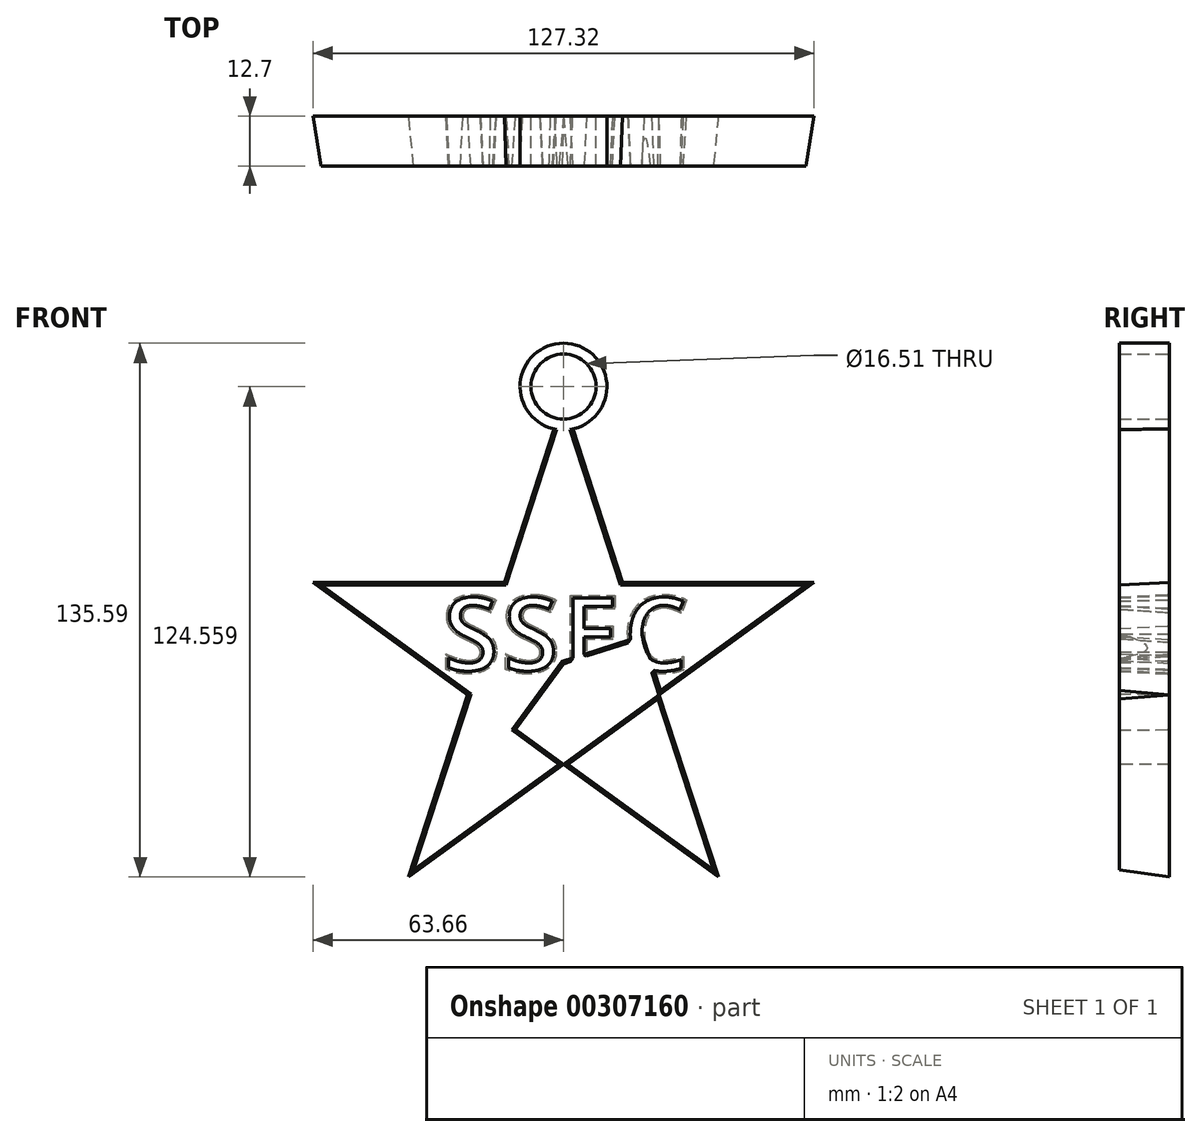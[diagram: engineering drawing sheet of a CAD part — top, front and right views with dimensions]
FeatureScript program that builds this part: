
annotation { "Feature Type Name" : "Feature", "Feature Type Description" : "" }
export const myFeature = defineFeature(function(context is Context, id is Id, definition is map)
    precondition{}
    {
        {
            var Q0;
            Q0=qCreatedBy(makeId("Front.planeOp"),FACE);
            var sketch = newSketch(context, id + "F0", { "sketchPlane" : qUnion([Q0])});
            skLineSegment(sketch, "E0", {"start": v(0, 66.94) * mm, "end": v(-39.35, -54.15) * mm});
            skLineSegment(sketch, "E1", {"start": v(-39.35, -54.15) * mm, "end": v(0, 66.94) * mm});
            skLineSegment(sketch, "E2", {"start": v(0, 66.94) * mm, "end": v(39.35, -54.15) * mm});
            skLineSegment(sketch, "E3", {"start": v(-39.35, -54.15) * mm, "end": v(63.66, 20.68) * mm});
            skLineSegment(sketch, "E4", {"start": v(63.66, 20.68) * mm, "end": v(-63.66, 20.68) * mm});
            skLineSegment(sketch, "E5", {"start": v(-63.66, 20.68) * mm, "end": v(39.35, -54.15) * mm});
            skLineSegment(sketch, "E6", {"start": v(-15.03, 20.68) * mm, "end": v(0, 0) * mm});
            skLineSegment(sketch, "E7", {"start": v(15.03, 20.68) * mm, "end": v(0, 0) * mm});
            skLineSegment(sketch, "E8", {"start": v(0, 0) * mm, "end": v(24.32, -7.9) * mm});
            skLineSegment(sketch, "E9", {"start": v(24.32, -7.9) * mm, "end": v(0, 0) * mm});
            skLineSegment(sketch, "E10", {"start": v(0, -25.57) * mm, "end": v(0, 0) * mm});
            skLineSegment(sketch, "E11", {"start": v(0, 0) * mm, "end": v(-24.32, -7.9) * mm});
            skLineSegment(sketch, "E12", {"start": v(-39.35, -54.15) * mm, "end": v(-12.16, -16.73) * mm});
            skLineSegment(sketch, "E13", {"start": v(-63.66, 20.68) * mm, "end": v(-19.67, 6.4) * mm});
            skLineSegment(sketch, "E14", {"start": v(0, 66.94) * mm, "end": v(0, 20.68) * mm});
            skLineSegment(sketch, "E15", {"start": v(63.66, 20.68) * mm, "end": v(19.67, 6.4) * mm});
            skLineSegment(sketch, "E16", {"start": v(39.35, -54.15) * mm, "end": v(12.16, -16.73) * mm});
            skLineSegment(sketch, "E17", {"start": v(0, 20.68) * mm, "end": v(0, 0) * mm});
            skLineSegment(sketch, "E18", {"start": v(0, 0) * mm, "end": v(0, -25.57) * mm});
            skLineSegment(sketch, "E19", {"start": v(0, 0) * mm, "end": v(19.67, 6.4) * mm});
            skLineSegment(sketch, "E20", {"start": v(-19.67, 6.4) * mm, "end": v(0, 0) * mm});
            skLineSegment(sketch, "E21", {"start": v(0, 0) * mm, "end": v(-12.16, -16.73) * mm});
            skLineSegment(sketch, "E22", {"start": v(0, 0) * mm, "end": v(12.16, -16.73) * mm});
            skSolve(sketch);
        }
        {
            var Q0;
            {var subQ0=sQuery(id+"F0.wireOp",EDGE,"E11");Q0=makeQuery(id+"F0.imprint","IMPRINT",FACE,{"disambiguationData":[TD([[makeQuery(id+"F0.imprint","IMPRINT",EDGE,{"derivedFrom":subQ0}),-1.0]])]});}
            var Q1;
            {var subQ0=sQuery(id+"F0.wireOp",EDGE,"E6");Q1=makeQuery(id+"F0.imprint","IMPRINT",FACE,{"disambiguationData":[TD([[makeQuery(id+"F0.imprint","IMPRINT",EDGE,{"derivedFrom":subQ0}),-1.0]])]});}
            var Q2;
            {var subQ0=sQuery(id+"F0.wireOp",EDGE,"E7");Q2=makeQuery(id+"F0.imprint","IMPRINT",FACE,{"disambiguationData":[TD([[makeQuery(id+"F0.imprint","IMPRINT",EDGE,{"derivedFrom":subQ0}),1.0]])]});}
            var Q3;
            {var subQ0=sQuery(id+"F0.wireOp",EDGE,"E9");Q3=makeQuery(id+"F0.imprint","IMPRINT",FACE,{"disambiguationData":[TD([[makeQuery(id+"F0.imprint","IMPRINT",EDGE,{"derivedFrom":subQ0}),-1.0]])]});}
            var Q4;
            {var subQ2=sQuery(id+"F0.wireOp",EDGE,"E18");Q4=makeQuery(id+"F0.imprint","IMPRINT",FACE,{"disambiguationData":[TD([[makeQuery(id+"F0.imprint","IMPRINT",EDGE,{"derivedFrom":subQ2}),1.0]])]});}
            var Q5;
            {var subQ0=sQuery(id+"F0.wireOp",EDGE,"E9");Q5=makeQuery(id+"F0.imprint","IMPRINT",FACE,{"disambiguationData":[TD([[makeQuery(id+"F0.imprint","IMPRINT",EDGE,{"derivedFrom":subQ0}),1.0]])]});}
            var Q6;
            {var subQ0=sQuery(id+"F0.wireOp",EDGE,"E6");Q6=makeQuery(id+"F0.imprint","IMPRINT",FACE,{"disambiguationData":[TD([[makeQuery(id+"F0.imprint","IMPRINT",EDGE,{"derivedFrom":subQ0}),1.0]])]});}
            var Q7;
            {var subQ0=sQuery(id+"F0.wireOp",EDGE,"E11");Q7=makeQuery(id+"F0.imprint","IMPRINT",FACE,{"disambiguationData":[TD([[makeQuery(id+"F0.imprint","IMPRINT",EDGE,{"derivedFrom":subQ0}),1.0]])]});}
            var Q8;
            {var subQ2=sQuery(id+"F0.wireOp",EDGE,"E18");Q8=makeQuery(id+"F0.imprint","IMPRINT",FACE,{"disambiguationData":[TD([[makeQuery(id+"F0.imprint","IMPRINT",EDGE,{"derivedFrom":subQ2}),-1.0]])]});}
            var Q9;
            {var subQ0=sQuery(id+"F0.wireOp",EDGE,"E14");Q9=makeQuery(id+"F0.imprint","IMPRINT",FACE,{"disambiguationData":[TD([[makeQuery(id+"F0.imprint","IMPRINT",EDGE,{"derivedFrom":subQ0}),1.0]])]});}
            var Q10;
            {var subQ3=sQuery(id+"F0.wireOp",EDGE,"E13");Q10=makeQuery(id+"F0.imprint","IMPRINT",FACE,{"disambiguationData":[TD([[makeQuery(id+"F0.imprint","IMPRINT",EDGE,{"derivedFrom":subQ3}),1.0]])]});}
            var Q11;
            {var subQ3=sQuery(id+"F0.wireOp",EDGE,"E13");Q11=makeQuery(id+"F0.imprint","IMPRINT",FACE,{"disambiguationData":[TD([[makeQuery(id+"F0.imprint","IMPRINT",EDGE,{"derivedFrom":subQ3}),-1.0]])]});}
            var Q12;
            {var subQ0=sQuery(id+"F0.wireOp",EDGE,"E12");Q12=makeQuery(id+"F0.imprint","IMPRINT",FACE,{"disambiguationData":[TD([[makeQuery(id+"F0.imprint","IMPRINT",EDGE,{"derivedFrom":subQ0}),1.0]])]});}
            var Q13;
            {var subQ0=sQuery(id+"F0.wireOp",EDGE,"E12");Q13=makeQuery(id+"F0.imprint","IMPRINT",FACE,{"disambiguationData":[TD([[makeQuery(id+"F0.imprint","IMPRINT",EDGE,{"derivedFrom":subQ0}),-1.0]])]});}
            var Q14;
            {var subQ0=sQuery(id+"F0.wireOp",EDGE,"E16");Q14=makeQuery(id+"F0.imprint","IMPRINT",FACE,{"disambiguationData":[TD([[makeQuery(id+"F0.imprint","IMPRINT",EDGE,{"derivedFrom":subQ0}),1.0]])]});}
            var Q15;
            {var subQ0=sQuery(id+"F0.wireOp",EDGE,"E16");Q15=makeQuery(id+"F0.imprint","IMPRINT",FACE,{"disambiguationData":[TD([[makeQuery(id+"F0.imprint","IMPRINT",EDGE,{"derivedFrom":subQ0}),-1.0]])]});}
            var Q16;
            {var subQ3=sQuery(id+"F0.wireOp",EDGE,"E15");Q16=makeQuery(id+"F0.imprint","IMPRINT",FACE,{"disambiguationData":[TD([[makeQuery(id+"F0.imprint","IMPRINT",EDGE,{"derivedFrom":subQ3}),1.0]])]});}
            var Q17;
            {var subQ3=sQuery(id+"F0.wireOp",EDGE,"E15");Q17=makeQuery(id+"F0.imprint","IMPRINT",FACE,{"disambiguationData":[TD([[makeQuery(id+"F0.imprint","IMPRINT",EDGE,{"derivedFrom":subQ3}),-1.0]])]});}
            var Q18;
            {var subQ0=sQuery(id+"F0.wireOp",EDGE,"E7");Q18=makeQuery(id+"F0.imprint","IMPRINT",FACE,{"disambiguationData":[TD([[makeQuery(id+"F0.imprint","IMPRINT",EDGE,{"derivedFrom":subQ0}),-1.0]])]});}
            var Q19;
            {var subQ0=sQuery(id+"F0.wireOp",EDGE,"E14");Q19=makeQuery(id+"F0.imprint","IMPRINT",FACE,{"disambiguationData":[TD([[makeQuery(id+"F0.imprint","IMPRINT",EDGE,{"derivedFrom":subQ0}),-1.0]])]});}
            extrude(context, id + "F1", {"entities" : qUnion([Q0, Q1, Q2, Q3, Q4, Q5, Q6, Q7, Q8, Q9, Q10, Q11, Q12, Q13, Q14, Q15, Q16, Q17, Q18, Q19]), "depth" : 12.7 * mm, "hasDraft" : true, "draftAngle" : 3 * degree, "draftPullDirection" : true});
        }
        {
            var Q0;
            Q0=qCreatedBy(makeId("Front.planeOp"),FACE);
            var sketch = newSketch(context, id + "F2", { "sketchPlane" : qUnion([Q0])});
            skText(sketch, "E23", { "text": "SSEC", "fontName": "OpenSans-Bold.ttf"});
            const initialGuessF2  = {"E23": [-0.03112, -0.00233, 1, 0, 0.01985]};
            skSetInitialGuess(sketch, initialGuessF2);
            skSolve(sketch);
        }
        {
            var Q0;
            Q0 = qSketchRegion(id + "F2", true);
            extrude(context, id + "F3", {"entities" : qUnion([Q0]), "operationType" : NewBodyOperationType.REMOVE, "depth" : 12.7 * mm, "hasDraft" : true, "draftAngle" : 3 * degree, "draftPullDirection" : true});
        }
        {
            var Q0;
            Q0=qCreatedBy(makeId("Front.planeOp"),FACE);
            var sketch = newSketch(context, id + "F4", { "sketchPlane" : qUnion([Q0])});
            skCircle(sketch, "E24", {"center": v(0, 70.4) * mm, "radius": 11.03 * mm});
            skSolve(sketch);
        }
        {
            var Q0;
            Q0 = qSketchRegion(id + "F4", true);
            extrude(context, id + "F5", {"entities" : qUnion([Q0]), "operationType" : NewBodyOperationType.ADD, "depth" : 12.7 * mm});
        }
        {
            var Q0;
            Q0=qCreatedBy(makeId("Front.planeOp"),FACE);
            var sketch = newSketch(context, id + "F6", { "sketchPlane" : qUnion([Q0])});
            skCircle(sketch, "E25", {"center": v(0, 70.4) * mm, "radius": 8.25 * mm});
            skSolve(sketch);
        }
        {
            var Q0;
            Q0 = qSketchRegion(id + "F6", true);
            extrude(context, id + "F7", {"entities" : qUnion([Q0]), "operationType" : NewBodyOperationType.REMOVE, "depth" : 12.7 * mm});
        }
    });
